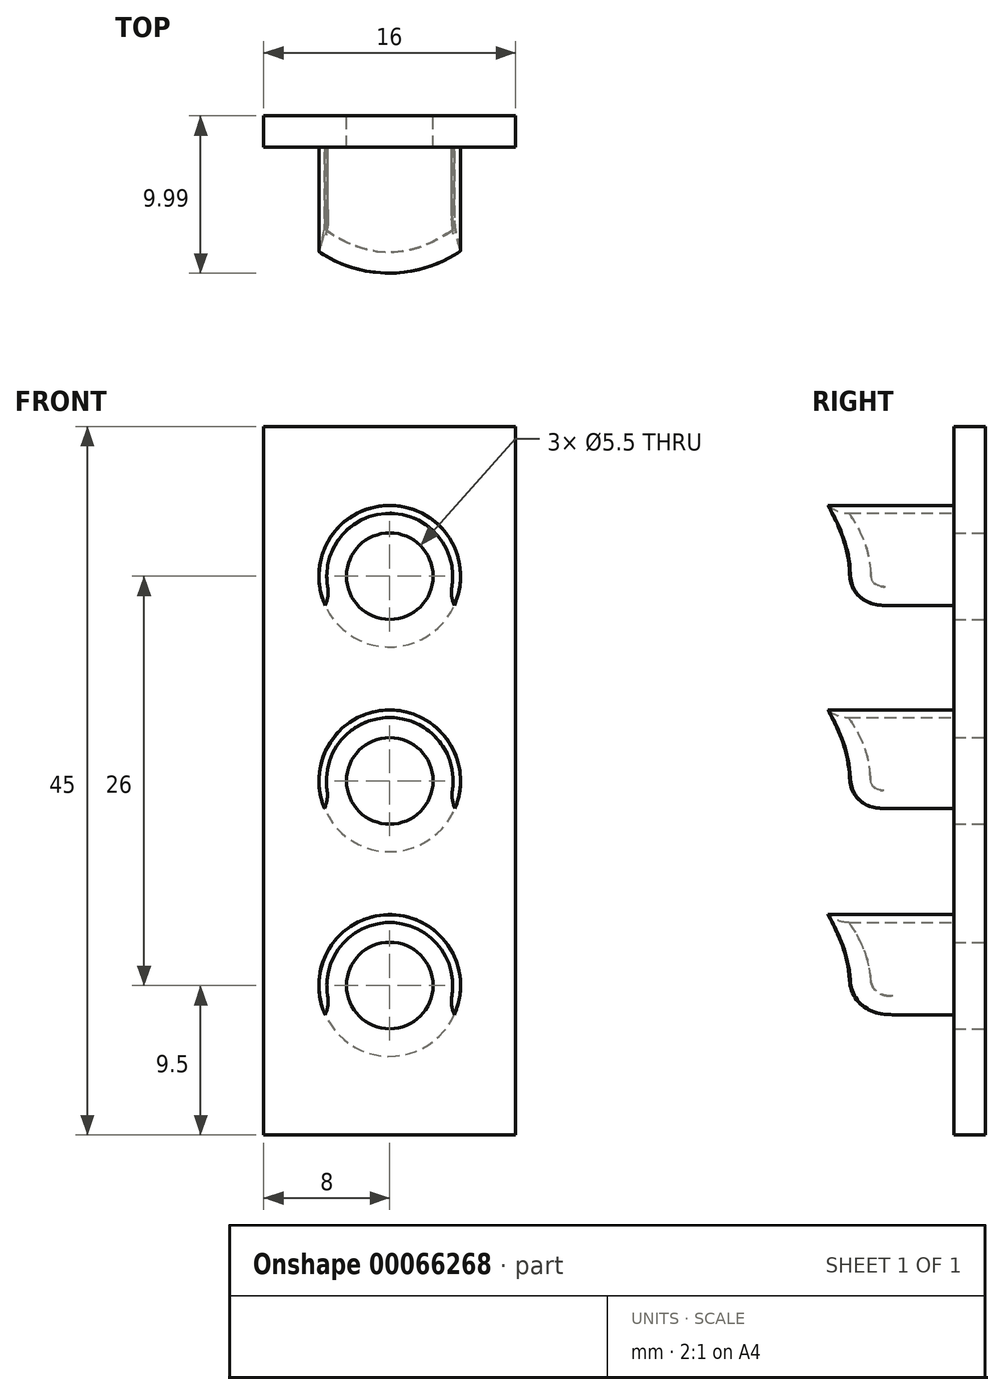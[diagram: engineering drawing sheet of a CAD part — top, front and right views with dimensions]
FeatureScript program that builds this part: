
annotation { "Feature Type Name" : "Feature", "Feature Type Description" : "" }
export const myFeature = defineFeature(function(context is Context, id is Id, definition is map)
    precondition{}
    {
        {
            var Q0;
            Q0=qCreatedBy(makeId("Front.planeOp"),FACE);
            var sketch = newSketch(context, id + "F0", { "sketchPlane" : qUnion([Q0])});
            skLineSegment(sketch, "E0", {"start": v(-8, 22.5) * mm, "end": v(8, 22.5) * mm});
            skLineSegment(sketch, "E1", {"start": v(8, 22.5) * mm, "end": v(8, -22.5) * mm});
            skLineSegment(sketch, "E2", {"start": v(8, -22.5) * mm, "end": v(-8, -22.5) * mm});
            skLineSegment(sketch, "E3", {"start": v(-8, -22.5) * mm, "end": v(-8, 22.5) * mm});
            skLineSegment(sketch, "E4", {"start": v(0, 22.5) * mm, "end": v(0, 0) * mm, "construction": true});
            skCircle(sketch, "E5", {"center": v(0, 0) * mm, "radius": 2.75 * mm});
            skCircle(sketch, "E6", {"center": v(0, 13) * mm, "radius": 2.75 * mm});
            skCircle(sketch, "E7", {"center": v(0, -13) * mm, "radius": 2.75 * mm});
            skLineSegment(sketch, "E8", {"start": v(0, 13) * mm, "end": v(0, 0) * mm, "construction": true});
            skLineSegment(sketch, "E9", {"start": v(0, 0) * mm, "end": v(0, -13) * mm, "construction": true});
            skLineSegment(sketch, "E10", {"start": v(8, 0) * mm, "end": v(8, 22.5) * mm});
            skLineSegment(sketch, "E11", {"start": v(8, 0) * mm, "end": v(-8, 0) * mm});
            skLineSegment(sketch, "E12", {"start": v(0, 0) * mm, "end": v(0, 0) * mm});
            skSolve(sketch);
        }
        {
            var Q0;
            Q0=makeQuery(id+"F0.imprint","IMPRINT",FACE,{"disambiguationData":[TD([[makeQuery(id+"F0.imprint","IMPRINT",EDGE,{"derivedFrom":sQuery(id+"F0.wireOp",EDGE,"E0")}),-1.0]])]});
            extrude(context, id + "F1", {"entities" : qUnion([Q0]), "depth" : 2 * mm});
        }
        {
            var Q0;
            Q0 = qSketchRegion(id + "F0", true);
            extrude(context, id + "F2", {"entities" : qUnion([Q0]), "operationType" : NewBodyOperationType.ADD, "depth" : 2 * mm});
        }
        {
            var Q0;
            Q0=makeQuery(id+"F1.opExtrude","CAP_FACE",FACE,{"disambiguationData":[OSD([sQuery(id+"F0.wireOp",EDGE,"E0"),sQuery(id+"F0.wireOp",EDGE,"E1"),sQuery(id+"F0.wireOp",EDGE,"E2"),sQuery(id+"F0.wireOp",EDGE,"E3"),sQuery(id+"F0.wireOp",EDGE,"E5"),sQuery(id+"F0.wireOp",EDGE,"E6"),sQuery(id+"F0.wireOp",EDGE,"E7")])],"isStart":false});
            var sketch = newSketch(context, id + "F3", { "sketchPlane" : qUnion([Q0])});
            skArc(sketch, "E13", {"start": v(0, 17) * mm, "mid": v(3.42, 15.07) * mm, "end": v(3.54, 11.14) * mm});
            skArc(sketch, "E14", {"start": v(0, 17) * mm, "mid": v(-3.42, 15.07) * mm, "end": v(-3.54, 11.14) * mm});
            skArc(sketch, "E15", {"start": v(0, 17.5) * mm, "mid": v(-3.78, 15.44) * mm, "end": v(-4.1, 11.14) * mm});
            skArc(sketch, "E16", {"start": v(0, 17.5) * mm, "mid": v(3.78, 15.44) * mm, "end": v(4.1, 11.14) * mm});
            skLineSegment(sketch, "E17", {"start": v(-4.1, 11.14) * mm, "end": v(-3.54, 11.14) * mm});
            skLineSegment(sketch, "E18", {"start": v(3.54, 11.14) * mm, "end": v(4.1, 11.14) * mm});
            skSolve(sketch);
        }
        {
            var Q0;
            Q0 = qSketchRegion(id + "F3", true);
            extrude(context, id + "F4", {"entities" : qUnion([Q0]), "operationType" : NewBodyOperationType.ADD, "depth" : 10 * mm});
        }
        {
            var Q0;
            {var subQ0=sQuery(id+"F0.wireOp",EDGE,"E10");var subQ1=sQuery(id+"F0.wireOp",EDGE,"E6");var subQ2=sQuery(id+"F0.wireOp",EDGE,"E5");var subQ3=sQuery(id+"F0.wireOp",EDGE,"E3");var subQ4=sQuery(id+"F0.wireOp",EDGE,"E0");Q0=makeQuery(id+"F2.boolean.opBoolean","MERGE",FACE,{"derivedFrom":[makeQuery(id+"F1.opExtrude","CAP_FACE",FACE,{"disambiguationData":[OSD([subQ4,subQ3,subQ2,subQ1,subQ0,sQuery(id+"F0.wireOp",EDGE,"E11")])],"isStart":false}),makeQuery(id+"F2.opExtrude","CAP_FACE",FACE,{"disambiguationData":[OSD([subQ4,sQuery(id+"F0.wireOp",EDGE,"E1"),sQuery(id+"F0.wireOp",EDGE,"E2"),subQ3,subQ2,subQ1,sQuery(id+"F0.wireOp",EDGE,"E7"),subQ0])],"isStart":false})]});}
            var sketch = newSketch(context, id + "F5", { "sketchPlane" : qUnion([Q0])});
            skArc(sketch, "E19", {"start": v(-0.45, 4) * mm, "mid": v(3.3, 2.3) * mm, "end": v(3.6, -1.8) * mm});
            skArc(sketch, "E20", {"start": v(-0.45, 4) * mm, "mid": v(-3.54, 1.92) * mm, "end": v(-3.6, -1.8) * mm});
            skArc(sketch, "E21", {"start": v(0, 4.5) * mm, "mid": v(-3.75, 2.49) * mm, "end": v(-4.15, -1.75) * mm});
            skArc(sketch, "E22", {"start": v(0, 4.5) * mm, "mid": v(3.75, 2.49) * mm, "end": v(4.15, -1.75) * mm});
            skLineSegment(sketch, "E23", {"start": v(-4.15, -1.75) * mm, "end": v(-3.6, -1.8) * mm});
            skLineSegment(sketch, "E24", {"start": v(3.6, -1.8) * mm, "end": v(4.15, -1.75) * mm});
            skSolve(sketch);
        }
        {
            var Q0;
            Q0 = qSketchRegion(id + "F5", true);
            extrude(context, id + "F6", {"entities" : qUnion([Q0]), "operationType" : NewBodyOperationType.ADD, "depth" : 10 * mm});
        }
        {
            var Q0;
            {var subQ0=sQuery(id+"F0.wireOp",EDGE,"E10");var subQ1=sQuery(id+"F0.wireOp",EDGE,"E6");var subQ2=sQuery(id+"F0.wireOp",EDGE,"E5");var subQ3=sQuery(id+"F0.wireOp",EDGE,"E3");var subQ4=sQuery(id+"F0.wireOp",EDGE,"E0");Q0=makeQuery(id+"F2.boolean.opBoolean","MERGE",FACE,{"derivedFrom":[makeQuery(id+"F1.opExtrude","CAP_FACE",FACE,{"disambiguationData":[OSD([subQ4,subQ3,subQ2,subQ1,subQ0,sQuery(id+"F0.wireOp",EDGE,"E11")])],"isStart":false}),makeQuery(id+"F2.opExtrude","CAP_FACE",FACE,{"disambiguationData":[OSD([subQ4,sQuery(id+"F0.wireOp",EDGE,"E1"),sQuery(id+"F0.wireOp",EDGE,"E2"),subQ3,subQ2,subQ1,sQuery(id+"F0.wireOp",EDGE,"E7"),subQ0])],"isStart":false})]});}
            var sketch = newSketch(context, id + "F7", { "sketchPlane" : qUnion([Q0])});
            skLineSegment(sketch, "E25", {"start": v(0, -13) * mm, "end": v(0, -8.5) * mm, "construction": true});
            skArc(sketch, "E26", {"start": v(0, -8.5) * mm, "mid": v(3.78, -10.56) * mm, "end": v(4.1, -14.85) * mm});
            skArc(sketch, "E27", {"start": v(0, -8.5) * mm, "mid": v(-3.78, -10.56) * mm, "end": v(-4.1, -14.85) * mm});
            skArc(sketch, "E28", {"start": v(0, -9) * mm, "mid": v(3.39, -10.88) * mm, "end": v(3.6, -14.74) * mm});
            skArc(sketch, "E29", {"start": v(0, -9) * mm, "mid": v(-3.39, -10.88) * mm, "end": v(-3.6, -14.74) * mm});
            skLineSegment(sketch, "E30", {"start": v(-4.1, -14.85) * mm, "end": v(-3.6, -14.74) * mm});
            skLineSegment(sketch, "E31", {"start": v(3.6, -14.74) * mm, "end": v(4.1, -14.85) * mm});
            skSolve(sketch);
        }
        {
            var Q0;
            Q0=qCreatedBy(makeId("Top.planeOp"),FACE);
            var sketch = newSketch(context, id + "F8", { "sketchPlane" : qUnion([Q0])});
            skLineSegment(sketch, "E32", {"start": v(-8, -9.41) * mm, "end": v(-8, -12.7) * mm});
            skLineSegment(sketch, "E33", {"start": v(-8, -2) * mm, "end": v(-8, -2) * mm});
            skLineSegment(sketch, "E34", {"start": v(7.92, -12.7) * mm, "end": v(-8, -12.7) * mm});
            skLineSegment(sketch, "E35", {"start": v(7.92, -12.7) * mm, "end": v(7.92, -2.06) * mm});
            skArc(sketch, "E36", {"start": v(-8, -2) * mm, "mid": v(-0.07, -10) * mm, "end": v(7.92, -2.06) * mm});
            skLineSegment(sketch, "E37", {"start": v(-8, -12.7) * mm, "end": v(-8, -2) * mm});
            skSolve(sketch);
        }
        {
            var Q0;
            Q0 = qSketchRegion(id + "F7", true);
            extrude(context, id + "F9", {"entities" : qUnion([Q0]), "operationType" : NewBodyOperationType.ADD, "depth" : 10 * mm});
        }
        {
            var Q0;
            Q0 = qSketchRegion(id + "F8", true);
            extrude(context, id + "F10", {"entities" : qUnion([Q0]), "operationType" : NewBodyOperationType.REMOVE, "depth" : 34.6 * mm});
        }
        {
            var Q0;
            Q0 = qSketchRegion(id + "F8", true);
            extrude(context, id + "F11", {"entities" : qUnion([Q0]), "operationType" : NewBodyOperationType.REMOVE, "oppositeDirection" : true, "depth" : 25 * mm});
        }
        {
            var Q0;
            {var subQ0=sQuery(id+"F8.wireOp",EDGE,"E36");Q0=makeQuery(id+"F10.boolean.opBoolean","INTERSECT",EDGE,{"derivedFrom":[makeQuery(id+"F4.opExtrude","SWEPT_FACE",FACE,{"disambiguationData":[OSD([sQuery(id+"F3.wireOp",EDGE,"E18")])]}),makeQuery(id+"F10.opExtrude","SWEPT_FACE",FACE,{"disambiguationData":[OSD([subQ0]),TDD([makeQuery(id+"F8.imprint","IMPRINT",EDGE,{"disambiguationData":[TD([[makeQuery(id+"F8.imprint","INTERSECT",VERTEX,{"disambiguationData":[OD(1.0)],"derivedFrom":[sQuery(id+"F8.wireOp",EDGE,"E35"),subQ0]}),1.0]])],"derivedFrom":subQ0})])]})]});}
            var Q1;
            {var subQ0=sQuery(id+"F8.wireOp",EDGE,"E36");Q1=makeQuery(id+"F11.boolean.opBoolean","INTERSECT",EDGE,{"derivedFrom":[makeQuery(id+"F6.opExtrude","SWEPT_FACE",FACE,{"disambiguationData":[OSD([sQuery(id+"F5.wireOp",EDGE,"E24")])]}),makeQuery(id+"F11.opExtrude","SWEPT_FACE",FACE,{"disambiguationData":[OSD([subQ0]),TDD([makeQuery(id+"F8.imprint","IMPRINT",EDGE,{"disambiguationData":[TD([[makeQuery(id+"F8.imprint","INTERSECT",VERTEX,{"derivedFrom":[sQuery(id+"F8.wireOp",EDGE,"E35"),subQ0]}),1.0]])],"derivedFrom":subQ0})])]})]});}
            var Q2;
            {var subQ0=sQuery(id+"F8.wireOp",EDGE,"E36");Q2=makeQuery(id+"F11.boolean.opBoolean","INTERSECT",EDGE,{"derivedFrom":[makeQuery(id+"F6.opExtrude","SWEPT_FACE",FACE,{"disambiguationData":[OSD([sQuery(id+"F5.wireOp",EDGE,"E23")])]}),makeQuery(id+"F11.opExtrude","SWEPT_FACE",FACE,{"disambiguationData":[OSD([subQ0]),TDD([makeQuery(id+"F8.imprint","IMPRINT",EDGE,{"disambiguationData":[TD([[makeQuery(id+"F8.imprint","INTERSECT",VERTEX,{"derivedFrom":[sQuery(id+"F8.wireOp",EDGE,"E35"),subQ0]}),1.0]])],"derivedFrom":subQ0})])]})]});}
            var Q3;
            {var subQ0=sQuery(id+"F8.wireOp",EDGE,"E36");Q3=makeQuery(id+"F10.boolean.opBoolean","INTERSECT",EDGE,{"derivedFrom":[makeQuery(id+"F4.opExtrude","SWEPT_FACE",FACE,{"disambiguationData":[OSD([sQuery(id+"F3.wireOp",EDGE,"E17")])]}),makeQuery(id+"F10.opExtrude","SWEPT_FACE",FACE,{"disambiguationData":[OSD([subQ0]),TDD([makeQuery(id+"F8.imprint","IMPRINT",EDGE,{"disambiguationData":[TD([[makeQuery(id+"F8.imprint","INTERSECT",VERTEX,{"derivedFrom":[sQuery(id+"F8.wireOp",EDGE,"E35"),subQ0]}),1.0]])],"derivedFrom":subQ0})])]})]});}
            var Q4;
            {var subQ0=sQuery(id+"F8.wireOp",EDGE,"E36");Q4=makeQuery(id+"F11.boolean.opBoolean","INTERSECT",EDGE,{"derivedFrom":[makeQuery(id+"F9.opExtrude","SWEPT_FACE",FACE,{"disambiguationData":[OSD([sQuery(id+"F7.wireOp",EDGE,"E30")])]}),makeQuery(id+"F11.opExtrude","SWEPT_FACE",FACE,{"disambiguationData":[OSD([subQ0]),TDD([makeQuery(id+"F8.imprint","IMPRINT",EDGE,{"disambiguationData":[TD([[makeQuery(id+"F8.imprint","INTERSECT",VERTEX,{"derivedFrom":[sQuery(id+"F8.wireOp",EDGE,"E35"),subQ0]}),1.0]])],"derivedFrom":subQ0})])]})]});}
            var Q5;
            {var subQ0=sQuery(id+"F8.wireOp",EDGE,"E36");Q5=makeQuery(id+"F11.boolean.opBoolean","INTERSECT",EDGE,{"derivedFrom":[makeQuery(id+"F9.opExtrude","SWEPT_FACE",FACE,{"disambiguationData":[OSD([sQuery(id+"F7.wireOp",EDGE,"E31")])]}),makeQuery(id+"F11.opExtrude","SWEPT_FACE",FACE,{"disambiguationData":[OSD([subQ0]),TDD([makeQuery(id+"F8.imprint","IMPRINT",EDGE,{"disambiguationData":[TD([[makeQuery(id+"F8.imprint","INTERSECT",VERTEX,{"derivedFrom":[sQuery(id+"F8.wireOp",EDGE,"E35"),subQ0]}),1.0]])],"derivedFrom":subQ0})])]})]});}
            fillet(context, id + "F12", {"entities" : qUnion([Q0, Q1, Q2, Q3, Q4, Q5]), "radius" : 2 * mm, "tangentPropagation" : true, "allowEdgeOverflow" : false});
        }
        {
            var Q0;
            {var subQ0=sQuery(id+"F8.wireOp",EDGE,"E36");Q0=makeQuery(id+"F10.boolean.opBoolean","INTERSECT",EDGE,{"derivedFrom":[makeQuery(id+"F4.opExtrude","SWEPT_FACE",FACE,{"disambiguationData":[OSD([sQuery(id+"F3.wireOp",EDGE,"E13"),sQuery(id+"F3.wireOp",EDGE,"E14")])]}),makeQuery(id+"F10.opExtrude","SWEPT_FACE",FACE,{"disambiguationData":[OSD([subQ0]),TDD([makeQuery(id+"F8.imprint","IMPRINT",EDGE,{"disambiguationData":[TD([[makeQuery(id+"F8.imprint","INTERSECT",VERTEX,{"disambiguationData":[OD(1.0)],"derivedFrom":[sQuery(id+"F8.wireOp",EDGE,"E35"),subQ0]}),1.0]])],"derivedFrom":subQ0})])]})]});}
            var Q1;
            {var subQ0=sQuery(id+"F8.wireOp",EDGE,"E36");Q1=makeQuery(id+"F11.boolean.opBoolean","INTERSECT",EDGE,{"derivedFrom":[makeQuery(id+"F6.opExtrude","SWEPT_FACE",FACE,{"disambiguationData":[OSD([sQuery(id+"F5.wireOp",EDGE,"E19"),sQuery(id+"F5.wireOp",EDGE,"E20")])]}),makeQuery(id+"F11.opExtrude","SWEPT_FACE",FACE,{"disambiguationData":[OSD([subQ0]),TDD([makeQuery(id+"F8.imprint","IMPRINT",EDGE,{"disambiguationData":[TD([[makeQuery(id+"F8.imprint","INTERSECT",VERTEX,{"derivedFrom":[sQuery(id+"F8.wireOp",EDGE,"E35"),subQ0]}),1.0]])],"derivedFrom":subQ0})])]})]});}
            var Q2;
            {var subQ0=sQuery(id+"F8.wireOp",EDGE,"E36");Q2=makeQuery(id+"F11.boolean.opBoolean","INTERSECT",EDGE,{"derivedFrom":[makeQuery(id+"F9.opExtrude","SWEPT_FACE",FACE,{"disambiguationData":[OSD([sQuery(id+"F7.wireOp",EDGE,"E28"),sQuery(id+"F7.wireOp",EDGE,"E29")])]}),makeQuery(id+"F11.opExtrude","SWEPT_FACE",FACE,{"disambiguationData":[OSD([subQ0]),TDD([makeQuery(id+"F8.imprint","IMPRINT",EDGE,{"disambiguationData":[TD([[makeQuery(id+"F8.imprint","INTERSECT",VERTEX,{"derivedFrom":[sQuery(id+"F8.wireOp",EDGE,"E35"),subQ0]}),1.0]])],"derivedFrom":subQ0})])]})]});}
            fillet(context, id + "F13", {"entities" : qUnion([Q0, Q1, Q2]), "radius" : 2 * mm, "tangentPropagation" : true, "allowEdgeOverflow" : false});
        }
    });
